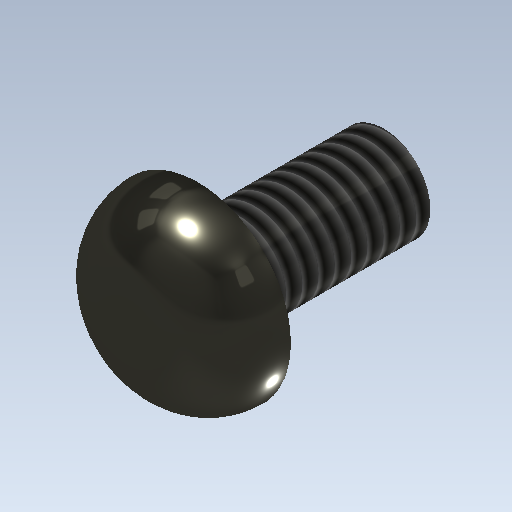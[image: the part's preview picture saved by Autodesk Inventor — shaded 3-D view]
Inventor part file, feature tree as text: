
AUTODESK INVENTOR PART (.ipt)
format: ipt  version: 2020.2 (Build 242310000, 310)  size: 175,104 bytes
history: native  units: mm
features: extrude x2, sketch x2, other x1, fillet x1, thread x1
ambient origin geometry x1: Origin
bodies: Body1 (feature_tree)
feature tree (7):
  other  "ソリッド1"
  extrude  "押し出し1"  Depth=4.0mm
  extrude  "押し出し2"  Depth=8.0mm TaperAngle=0.0deg
  fillet  "フィレット1"  Radius=8.0mm
  thread  "ねじ1"
  sketch  "スケッチ1"
  sketch  "スケッチ2"
